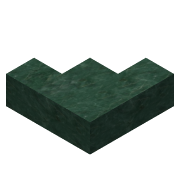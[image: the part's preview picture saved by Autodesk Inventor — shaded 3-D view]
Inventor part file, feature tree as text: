
AUTODESK INVENTOR PART (.ipt)
format: ipt  version: 2015 (Build 190159000, 159)  size: 110,080 bytes
history: native  units: in
note: dims shown in document units (in); Inventor stores cm internally (conversion verified against a paired STEP export)
features: extrude x1, sketch x1
ambient origin geometry x8: Origin, YZ Plane, XZ Plane, XY Plane, X Axis, Y Axis, Z Axis, Center Point
bodies: Solid1 (feature_tree)
feature tree (2):
  extrude  "Extrusion1"  Depth=1.0in
  sketch  "Sketch1"  dims[d0=3.0in d1=1.0in d2=1.0in d3=1.0in d4=1.0in d5=1.0in d6=1.0in d7=0.0in]
